# Revit family: QF_BPRO_BPT E 2 x 36_30 duo H_C banquet_575218
name_source: partatom
category: Sonderausstattung
revit_build: Autodesk Revit 2018 (Build: 20180423_1000(x64)
units: mm (PartAtom-declared; Revit-internal decimal feet)

## family parameters
Arbeitsebenenbasiert = Nein
Beim Laden mit Abzugskörper schneiden = Nein
Bemaßung runder Anschluss = Durchmesser verwenden
Gemeinsam genutzt = Nein
Immer vertikal = Ja
Raumberechnungspunkt = Nein
Teiletyp = Normal

## types (1)
- BPT E 2 x 36 (30) duo H/C banquet
    Accessory = Ja
    Beschreibung = BPT E 2 x 36 (30) duo heated / cooled banquet
2-compartment B.PROTHERM E banquet
trolley made of stainless less, mobile, 4 steering
castors, 2 of which have brakes; castors
160 mm dia., galvanised steel,
left compartment: convection-heated,
temperature range: +30 °C to +95 °C,
right Compartment: convection-cooled,
temperature range: +2 °C to +10 °C,
refrigerant: propane R290
    CE Approved = Ja
    Conn Conduit = Ja
    Conn Plug = Schuko plug
    Cycle = 50 Hz
    Depth Actual = 941 mm
    Electric power = 1360 W
    Foodservice Equipment Identifier = Ja
    Height Actual = 1795 mm
    Hersteller = B.PRO GmbH
    Item Number = 575218
    Kosten = 11800 $
    Length Actual = 1436 mm  [stored 4.71129 ft]
    Main switch integrated = Ja
    Masterspec = B.PROTHERM BPT E 2 x 36 (30) duo H/C banquet


Dimensions

Length:				 1436 mm
Width:			   941 mm
Height:			 1795 mm


Model

Design
The B.PROTHERM is made of AISI 304 stainless steel. The surface is micro-polished.  
The body and the hinged doors are double-walled and fitted with CFC-free PUR foam panels to provide thermal insulation. As a duo model, the trolley features two separate, thermally insulated compartments side by side.
The left compartment is convection-heated while the right compartment is convection-cooled. The compartments can be adjusted separately. The B.PROTHERM trolley is mobile thanks to galvanised steel castors (4 steering castors, 2 of which have brakes, castor diameter 160 mm). The sturdy, synthetic base structure with integrated all-round bumper rail protects the unit and furniture from damage.

Body
The base and rear and side walls are fitted with all-round edge radius R2 and are spot-welded at their points of contact (hygienic type HS). The interior is fully equipped with 36 pairs of deep-drawn stainless steel ledge walls per compartment for easy cleaning and maximum hygiene. The support ledges have a uniform spacing of 38.3 mm and are designed to safely hold Gastronorm grates size 2/1 and Gastronorm containers size GN 2/1 or 1/1 (crosswise insertion). This means all common spacing dimensions (about 75 mm, 115 mm) can be housed in a single unit and ensures efficient use of the interior. 
In the right compartment, the support ledges in front of the refrigeration compartment can also be used thanks to the intelligent positioning of the refrigeration compartment on the rear panel in the lower interior. This means that 30 pairs of support ledges are provided to hold size GN 2/1 or its subdivisions and 6 pairs of support ledges are provided to hold size GN 1/2 or its subdivisions.

The refrigeration unit is located in the body interior, protected by its outer casing. The refrigeration unit takes in air at the unit rear with the air inlet protected from dirt ingress and splashed water by a ventilation grate and air filter. The air exhaust outlet is located on the unit's lower surface. The B.PROTHERM interior contains a finned evaporator and a fan, which distributes the cold air uniformly in the unit interior through the evaporator via the air baffle integrated in the rear panel.
The active convection cooling is suitable for keeping food cold at a maximum temperature between +2 °C and +10 °C, as required for hygiene reasons.

The heating module with convection heating is permanently fitted into the left compartment's rear panel. Control range: +30 °C to +95 °C. The temperature can be regulated down to the degree in each compartment.   

On the rear panel of the interior body, an air baffle ensures optimum, rapid, uniform air circulation throughout the interior and also serves as a stop for inserted GN containers. 

The air baffle can be removed for cleaning purposes. 

Interior and exterior body are vertically connected with synthetic profiles and thermally separated.


The B.PROTHERM is equipped with 4 vertical push handles as standard to ensure optimum handling on all sides. 
 The ergonomic length of the handles makes the trolley easy to manoeuvre. 
The push handles are located within the bumper rail to prevent the hands from being crushed when rolling through doors and narrow corridors. The helix cord and plug holder are attached on the unit rear and also within the all-round bumper rail.

A B.PRO controller is integrated into the top of the unit above each compartment, ensuring user-friendly operation. It contains the unit on/off button, a menu button, a function button and an up/down button to precisely regulate the temperature in the interior concerned among other things. 

Doors
The trolley is equipped with two doors on its front that can be opened 270° and features a lock on its bottom plate. The doors are inside the bumper rail when open or closed and are thus protected from damage. The push handles are still accessible when the door is open. The robust door hinges are made of stainless steel investment casting. The hinge design eliminates risk of injury if a user should accidentally take hold of the hinge.
The doors are also fitted with an all-round, food-safe seal (TPE) that closes against the trolley body and can be removed. 
The built-in door contact switch ensures that refrigeration or heating switches off when the door is open, thus preventing unnecessary energy loss. 


The doors are fitted with a 2-point locking system. It is easy to open from the outside by simply pushing up the door handle. 
The B.PROTHERM has a push-button which glows in the dark in its interior. The patented 
panic opening can be identified if someone should get accidentally locked inside the interior and the door lock can be unlocked from the inside by pressing the button. What is known as the afterglow effect meets the requirements for safety-relevant components specified in ISO 16069. 


Options

•	Can be customised with powder coating on body and doors in 12 colours
•	Digitisation/connectivity for digital hygiene, temperature and process management using optionally built-in sensor technology 
•	Top with stainless steel railing on 3 sides
•	Top with stainless steel railing on 4 sides
•	Hygienic type H1
•	Door, lockable
•	Moisture system
•	Viewing panel
•	Draw bar and coupling made of stainless steel
•	Convenient door opening with foot operation
•	Galvanised steel castors, 160 mm in diameter, 
2 fixed and 2 steering castors with brakes 
•	Galvanised steel castors, 200 mm in diameter, 
2 fixed and 2 steering castors with brakes 
•	Galvanised steel castors, 200 mm in diameter, 
4 steering castors, 2 of which have brakes
•	Stainless-steel castors with elastic tyres, 160 mm in diameter, 4 steering castors, 2 of which have brakes 
•	Stainless-steel castors with elastic tyres, 160 mm in diameter, 2 fixed and 2 steering castors with brake 
•	Stainless-steel castors with elastic tyres, 200 mm in diameter, 2 fixed and 2 steering castors with brake 
•	Stainless-steel castors with elastic tyres, 200 mm in diameter, 4 steering castors, 2 of which have brakes 


Accessories

•	Eutectic plate -3 °C, synthetic 
(order no. 568 136)
•	Eutectic plate -12 °C, synthetic 
(order no. 573 332)
•	Slide-in frame to sub-divide GN containers
with max. depth 150 mm (order no. 564 352)
•	GN support bars for variable insertion of GN containers of the size GN 1/4, GN 1/6, GN 1/9 in the slide-in frame (ST 3 order no. 550 650; ST 5 order no. 550 651)
•	Menu card holder for the door on front, stainless steel, to attach DIN A5 and DIN A6 menu cards (order no. 575 230)
•	BPT E menu card, DIN A6 (order no. 564 353) 
•	Special pen for marking BPT E menu cards (order no. 564 361)
•	Menu card box, synthetic (order no. 564 355)

 
Technical data

Material:	Stainless steel,
	synthetic
Insulating material:		PUR foam panels, CFC-free 
Weight:	260 kg
Capacity:
•	Left compartment: 
18 x GN 2/1-65
•	Right compartment: 
15 x GN 2/1-65 + 3 x GN 1/1-65
Ledges:
•	Left compartment: 
36 pairs of deep-drawn support ledges
•	Right compartment: 
36 deep-drawn support ledges: 30 x 1/1 and 6 x 1/1 GN
	Space between ledges of 
	38.3 mm
Protection type: 	IPX5
Connected load:	220–240 V AC/50–60 Hz/ 
	1.36 kW
Temperature range:	
•	Left compartment: 
+30 °C to +95 °C*
•	Right compartment: can be regulated down to the degree from +2°C to +10 °C at an ambient temperature between +15 °C and +38 °C
Refrigerant:	Propane R290
Refrigerating capacity:		0.55 kW at t0= -10 °C and 
tu= +38 °C 
Climate class: 	4
Emissions:	The workplace-specific 
noise level for the unit is 
less than 70 dB(A)
* Measured at the container's geometrical centre






 
Special features

•	Two thermally separated compartments for different temperature ranges 
•	Extremely efficient, flexible use of interior thanks to uniform space between ledges of 38.3 mm
•	Deep-drawn stainless steel ledge walls for easy cleaning and maximum hygiene
•	Sturdy, enclosed, solid, synthetic base structure with integrated all-round bumper rail
•	Hinged door with door opening of 270°, with lock 
•	Optional connectivity function 


Make

Manufacturer:			B.PRO
Model:	BPT E 2 x 36 (30) duo H/C banquet
	B.PROTHERM
Order no.			575 218
    Material = QF_Metal-Stainless-Steel_general
    Material Rollen = QF_Metal-Stainless-Steel_general
    Material Stoßschutz = QF_Plastic-Black-Matt
    Model Warning = Upright transport position
Transport the unit in an upright position only.
The unit must not be operated during transport.
If the unit was not transported upright, wait 2 hours before commissioning.
Transport with a truck or delivery vehicle
The unit may only be transported in a truck or delivery vehicle which features a loading ramp.
The loading ramp must not exceed an angle of inclination of 10°.
The unit is not properly secured for transport if only the castor brakes have been applied.
Secure the unit on all four sides to prevent it from shifting.
Secure the unit against vertical movement during transport.
Use padded locking bars.
Commissioning after storage
Fire hazard
Pull off any protective film when unpacking the unit, as this presents a fire danger.
Electric shock due to electrical charge, danger of short-circuit
When the unit is brought from a cold storage room to a kitchen, moisture from the air in the room
condenses on the surface of the unit.
Steam can cause moisture condensation on the unit.
When the unit is connected to the power, there is a danger of the resulting moisture film causing
a short-circuit or an electric shock.
 Only operate the unit once it has reached room temperature.
 The unit may only be operated on a level, firm surface.
 Never operate the unit next to equipment which emits large amounts of steam, such as a
dishwasher.
 Set up/operate the unit in a well-ventilated environment only.
Blocked ventilation slits can cause the refrigeration unit to overheat and fail.
Keep the ventilation slits clear. Ventilation slits must be at least 10 cm from a wall when the
refrigeration unit is switched on.
The refrigerant propane (R290) is highly flammable and explosive (refrigerant group A3 according
to DIN EN 378‑2). In the event of a leak, an ignitable gas-air mixture can be produced which can
trigger an explosive reaction if the critical mixing ratio is reached and there is a suitable source of
ignition source.
Detailed safety information can be found in the operating instructions.
    Modell = BPT E 2 x 36 (30) duo H/C banquet
    Sound Level = < 70 dB(A)
    Typenkommentare = food transport container convection-heated and convection-cooled
    URL = https://www.bpro-solutions.com
    URL Manufacturer = https://www.bpro-solutions.com
    URL Recommended Spares List = https://www.bpro-solutions.com
    Volts = 220 V
    Weight = 260.00 kg

note: [stored X ft] marks values corroborated as IEEE doubles in the binary element streams (Revit-internal decimal feet)
